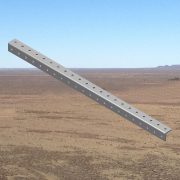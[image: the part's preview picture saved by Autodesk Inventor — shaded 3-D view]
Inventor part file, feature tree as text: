
AUTODESK INVENTOR PART (.ipt)
format: ipt  version: 2014 SP1 (Build 180222100, 222)  size: 184,320 bytes
history: native  units: in
note: dims shown in document units (in); Inventor stores cm internally (conversion verified against a paired STEP export)
features: sketch x3, hole x2, pattern_linear x2, extrude x1
ambient origin geometry x8: Origin, YZ Plane, XZ Plane, XY Plane, X Axis, Y Axis, Z Axis, Center Point
bodies: Solid1 (feature_tree)
feature tree (8):
  extrude  "Extrusion1"  Depth=1.0in
  hole  "Hole1"  [1 undecoded]
  pattern_linear  "Rectangular Pattern1"  Count1=24 Spacing1=1.0in
  hole  "Hole2"  [1 undecoded]
  pattern_linear  "Rectangular Pattern2"  Count1=24 Spacing1=1.0in
  sketch  "Sketch1"  dims[d0=1.0in d1=1.0in]
  sketch  "Sketch2"  dims[d2=0.125in d3=22.0in d4=0.0in]
  sketch  "Sketch3"  dims[d5=0.5in d6=0.25in d7=0.75in d8=0.375in d9=0.25in d10=0.5635in d11=1.0in d12=0.8108in d13=9.4488in d15=1.0in d16=0.5in d17=0.25in d18=0.75in d19=0.375in d20=0.25in d21=0.5635in d22=1.0in d23=0.8108in d24=9.4488in d26=1.0in]
note: 2 required parameter values undecoded (feature->parameter linkage not recoverable at this tier; creation-order binding heuristic only, values carry confidence <= 0.55)
